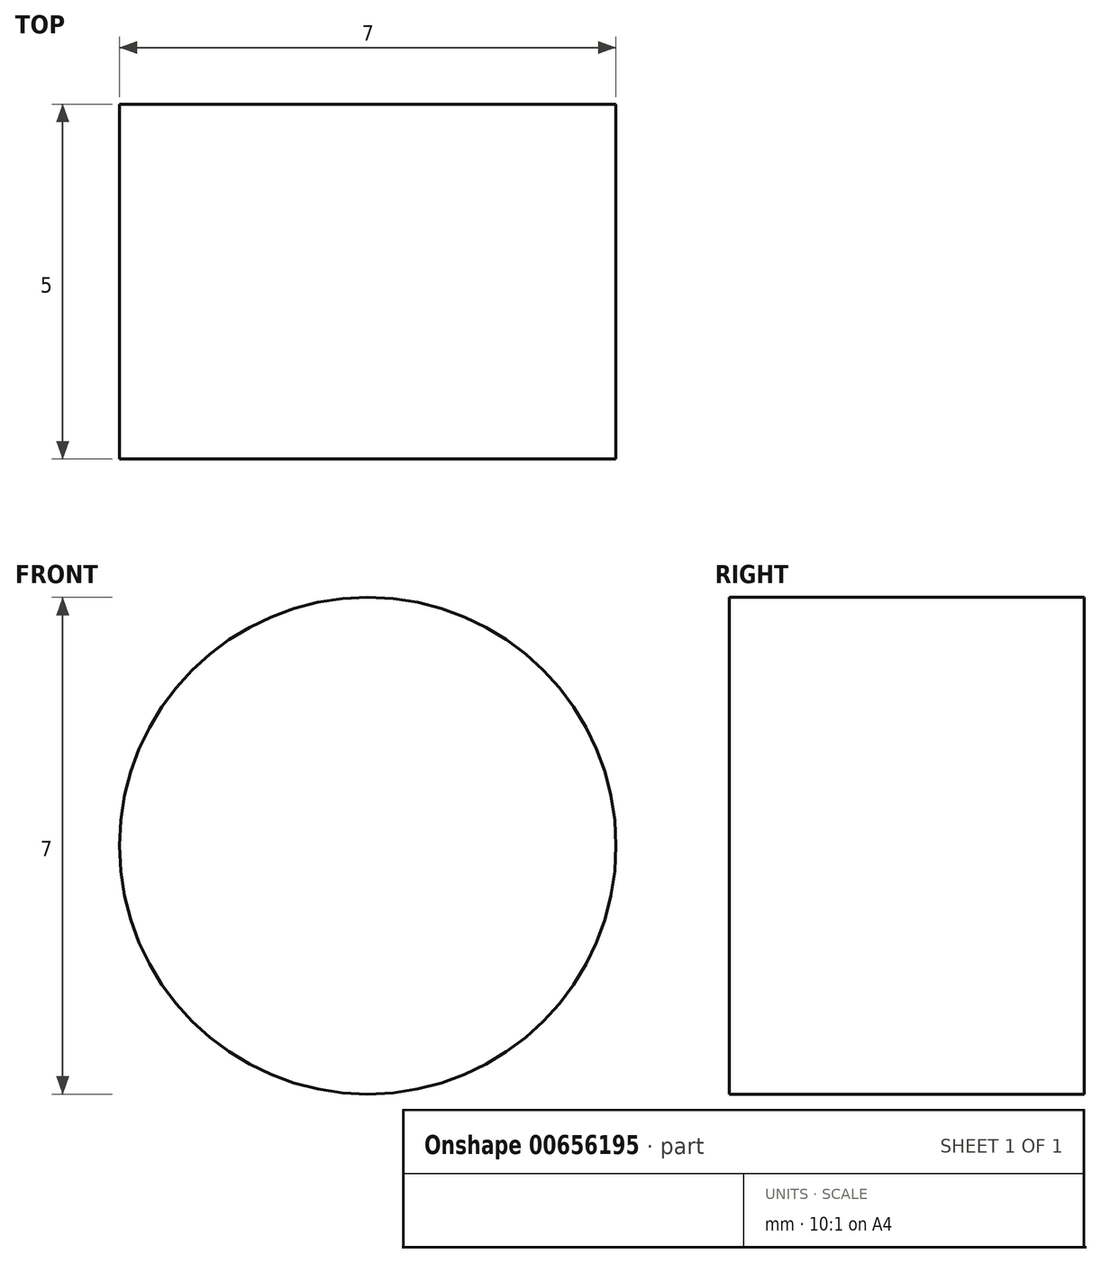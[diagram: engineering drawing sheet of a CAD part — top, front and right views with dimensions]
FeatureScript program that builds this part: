
annotation { "Feature Type Name" : "Feature", "Feature Type Description" : "" }
export const myFeature = defineFeature(function(context is Context, id is Id, definition is map)
    precondition{}
    {
        {
            var Q0;
            Q0=qCreatedBy(makeId("Front.planeOp"),FACE);
            var sketch = newSketch(context, id + "F0", { "sketchPlane" : qUnion([Q0])});
            skCircle(sketch, "E0", {"center": v(0, 0) * mm, "radius": 3.5 * mm});
            skSolve(sketch);
        }
        {
            var Q0;
            Q0=makeQuery(id+"F0.imprint","IMPRINT",FACE,{"disambiguationData":[TD([[makeQuery(id+"F0.imprint","IMPRINT",EDGE,{"derivedFrom":sQuery(id+"F0.wireOp",EDGE,"E0")}),1.0]])]});
            extrude(context, id + "F1", {"entities" : qUnion([Q0]), "depth" : 5 * mm, "offsetDistance" : 25 * mm});
        }
    });
